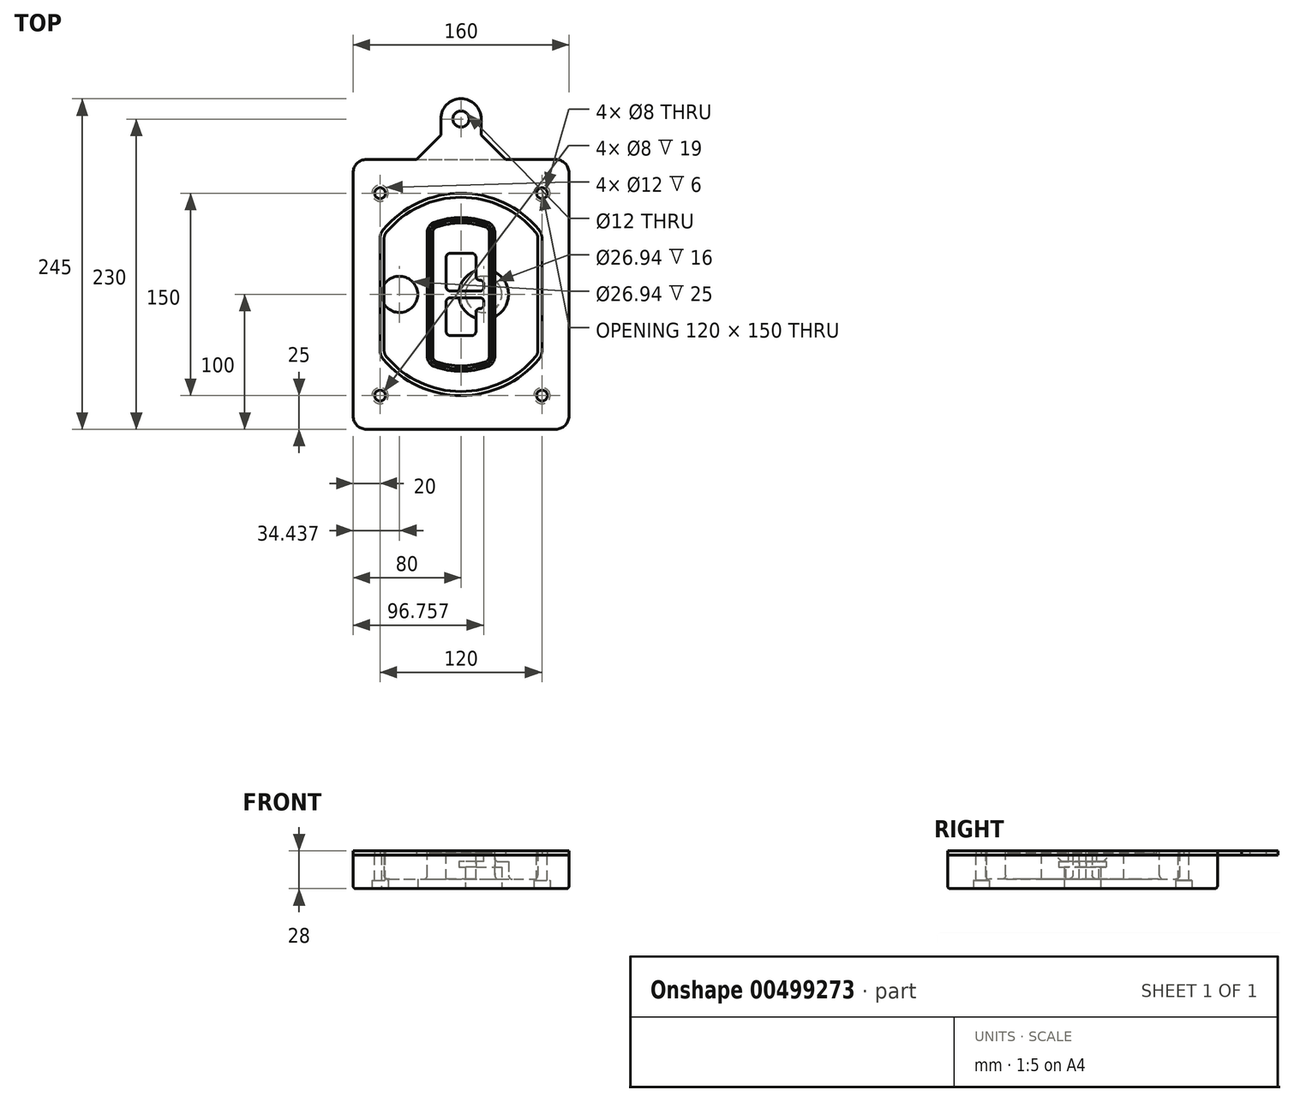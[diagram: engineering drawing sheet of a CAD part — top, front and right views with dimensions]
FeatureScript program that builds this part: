
annotation { "Feature Type Name" : "Feature", "Feature Type Description" : "" }
export const myFeature = defineFeature(function(context is Context, id is Id, definition is map)
    precondition{}
    {
        {
            var Q0;
            Q0=qCreatedBy(makeId("Top.planeOp"),FACE);
            var sketch = newSketch(context, id + "F0", { "sketchPlane" : qUnion([Q0])});
            skPoint(sketch, "E0.rect.middle", {"position": v(0, 0) * mm});
            skLineSegment(sketch, "E1.bottom", {"start": v(-70, -100) * mm, "end": v(70, -100) * mm});
            skLineSegment(sketch, "E1.top", {"start": v(-70, 100) * mm, "end": v(70, 100) * mm});
            skLineSegment(sketch, "E1.left", {"start": v(-80, -90) * mm, "end": v(-80, 90) * mm});
            skLineSegment(sketch, "E1.right", {"start": v(80, -90) * mm, "end": v(80, 90) * mm});
            skLineSegment(sketch, "E2", {"start": v(-80, 100) * mm, "end": v(80, -100) * mm, "construction": true});
            skLineSegment(sketch, "E3", {"start": v(80, 100) * mm, "end": v(-80, -100) * mm, "construction": true});
            skCircle(sketch, "E4", {"center": v(-60, 75) * mm, "radius": 4 * mm});
            skCircle(sketch, "E5", {"center": v(60, 75) * mm, "radius": 4 * mm});
            skCircle(sketch, "E6", {"center": v(60, -75) * mm, "radius": 4 * mm});
            skCircle(sketch, "E7", {"center": v(-60, -75) * mm, "radius": 4 * mm});
            skLineSegment(sketch, "E8", {"start": v(-60, 75) * mm, "end": v(60, 75) * mm, "construction": true});
            skLineSegment(sketch, "E9", {"start": v(60, 75) * mm, "end": v(60, -75) * mm, "construction": true});
            skLineSegment(sketch, "E10", {"start": v(60, -75) * mm, "end": v(-60, -75) * mm, "construction": true});
            skLineSegment(sketch, "E11", {"start": v(-60, -75) * mm, "end": v(-60, 75) * mm, "construction": true});
            skLineSegment(sketch, "E12", {"start": v(-60, 41.53) * mm, "end": v(-60, -41.53) * mm});
            skLineSegment(sketch, "E13", {"start": v(60, 41.53) * mm, "end": v(60, -41.53) * mm});
            skArc(sketch, "E14", {"start": v(57.7, 47.92) * mm, "mid": v(0, 75) * mm, "end": v(-57.7, 47.92) * mm});
            skArc(sketch, "E15", {"start": v(-57.7, -47.92) * mm, "mid": v(0, -75) * mm, "end": v(57.7, -47.92) * mm});
            skLineSegment(sketch, "E16", {"start": v(-60, 0) * mm, "end": v(60, 0) * mm, "construction": true});
            skPoint(sketch, "E17.visualSharp", {"position": v(-60, -45) * mm});
            skArc(sketch, "E17.filletArc", {"start": v(-60, -41.53) * mm, "mid": v(-59.4, -44.93) * mm, "end": v(-57.7, -47.92) * mm});
            skPoint(sketch, "E18.visualSharp", {"position": v(-60, 45) * mm});
            skArc(sketch, "E18.filletArc", {"start": v(-57.7, 47.92) * mm, "mid": v(-59.4, 44.93) * mm, "end": v(-60, 41.53) * mm});
            skPoint(sketch, "E19.visualSharp", {"position": v(60, 45) * mm});
            skArc(sketch, "E19.filletArc", {"start": v(60, 41.53) * mm, "mid": v(59.4, 44.93) * mm, "end": v(57.7, 47.92) * mm});
            skPoint(sketch, "E20.visualSharp", {"position": v(60, -45) * mm});
            skArc(sketch, "E20.filletArc", {"start": v(57.7, -47.92) * mm, "mid": v(59.4, -44.93) * mm, "end": v(60, -41.53) * mm});
            skPoint(sketch, "E21.visualSharp", {"position": v(-80, 100) * mm});
            skArc(sketch, "E21.filletArc", {"start": v(-70, 100) * mm, "mid": v(-77.07, 97.07) * mm, "end": v(-80, 90) * mm});
            skPoint(sketch, "E22.visualSharp", {"position": v(80, 100) * mm});
            skArc(sketch, "E22.filletArc", {"start": v(80, 90) * mm, "mid": v(77.07, 97.07) * mm, "end": v(70, 100) * mm});
            skPoint(sketch, "E23.visualSharp", {"position": v(80, -100) * mm});
            skArc(sketch, "E23.filletArc", {"start": v(70, -100) * mm, "mid": v(77.07, -97.07) * mm, "end": v(80, -90) * mm});
            skPoint(sketch, "E24.visualSharp", {"position": v(-80, -100) * mm});
            skArc(sketch, "E24.filletArc", {"start": v(-80, -90) * mm, "mid": v(-77.07, -97.07) * mm, "end": v(-70, -100) * mm});
            skArc(sketch, "E25.0", {"start": v(57, 41.53) * mm, "mid": v(56.58, 43.91) * mm, "end": v(55.38, 46) * mm});
            skLineSegment(sketch, "E25.1", {"start": v(57, 41.53) * mm, "end": v(57, -41.53) * mm});
            skArc(sketch, "E25.2", {"start": v(55.38, -46) * mm, "mid": v(56.58, -43.91) * mm, "end": v(57, -41.53) * mm});
            skArc(sketch, "E25.3", {"start": v(-55.38, -46) * mm, "mid": v(0, -72) * mm, "end": v(55.38, -46) * mm});
            skArc(sketch, "E25.4", {"start": v(-57, -41.53) * mm, "mid": v(-56.58, -43.91) * mm, "end": v(-55.38, -46) * mm});
            skArc(sketch, "E25.5", {"start": v(55.38, 46) * mm, "mid": v(0, 72) * mm, "end": v(-55.38, 46) * mm});
            skLineSegment(sketch, "E25.6", {"start": v(-57, 41.53) * mm, "end": v(-57, -41.53) * mm});
            skArc(sketch, "E25.7", {"start": v(-55.38, 46) * mm, "mid": v(-56.58, 43.91) * mm, "end": v(-57, 41.53) * mm});
            skArc(sketch, "E26.0", {"start": v(-60.77, 50.48) * mm, "mid": v(-63.17, 46.29) * mm, "end": v(-64, 41.53) * mm});
            skArc(sketch, "E26.1", {"start": v(60.77, 50.48) * mm, "mid": v(0, 79) * mm, "end": v(-60.77, 50.48) * mm});
            skArc(sketch, "E26.2", {"start": v(64, 41.53) * mm, "mid": v(63.17, 46.29) * mm, "end": v(60.77, 50.48) * mm});
            skLineSegment(sketch, "E26.3", {"start": v(64, 41.53) * mm, "end": v(64, -41.53) * mm});
            skArc(sketch, "E26.4", {"start": v(60.77, -50.48) * mm, "mid": v(63.17, -46.29) * mm, "end": v(64, -41.53) * mm});
            skLineSegment(sketch, "E26.5", {"start": v(-64, 41.53) * mm, "end": v(-64, -41.53) * mm});
            skArc(sketch, "E26.6", {"start": v(-60.77, -50.48) * mm, "mid": v(0, -79) * mm, "end": v(60.77, -50.48) * mm});
            skArc(sketch, "E26.7", {"start": v(-64, -41.53) * mm, "mid": v(-63.17, -46.29) * mm, "end": v(-60.77, -50.48) * mm});
            skSolve(sketch);
        }
        {
            var Q0;
            Q0=makeQuery(id+"F0.imprint","IMPRINT",FACE,{"disambiguationData":[TD([[makeQuery(id+"F0.imprint","IMPRINT",EDGE,{"derivedFrom":sQuery(id+"F0.wireOp",EDGE,"E1.bottom")}),1.0]])]});
            var Q1;
            Q1=makeQuery(id+"F0.imprint","IMPRINT",FACE,{"disambiguationData":[TD([[makeQuery(id+"F0.imprint","IMPRINT",EDGE,{"derivedFrom":sQuery(id+"F0.wireOp",EDGE,"E12")}),1.0]])]});
            var Q2;
            Q2=makeQuery(id+"F0.imprint","IMPRINT",FACE,{"disambiguationData":[TD([[makeQuery(id+"F0.imprint","IMPRINT",EDGE,{"derivedFrom":sQuery(id+"F0.wireOp",EDGE,"E25.0")}),1.0]])]});
            var Q3;
            Q3=makeQuery(id+"F0.imprint","IMPRINT",FACE,{"disambiguationData":[TD([[makeQuery(id+"F0.imprint","IMPRINT",EDGE,{"derivedFrom":sQuery(id+"F0.wireOp",EDGE,"E12")}),-1.0]])]});
            extrude(context, id + "F1", {"entities" : qUnion([Q0, Q1, Q2, Q3]), "oppositeDirection" : true, "depth" : 25 * mm});
        }
        {
            var Q0;
            Q0=makeQuery(id+"F0.imprint","IMPRINT",FACE,{"disambiguationData":[TD([[makeQuery(id+"F0.imprint","IMPRINT",EDGE,{"derivedFrom":sQuery(id+"F0.wireOp",EDGE,"E12")}),1.0]])]});
            extrude(context, id + "F2", {"entities" : qUnion([Q0]), "operationType" : NewBodyOperationType.ADD, "depth" : 3 * mm});
        }
        {
            var Q0;
            Q0=makeQuery(id+"F0.imprint","IMPRINT",FACE,{"disambiguationData":[TD([[makeQuery(id+"F0.imprint","IMPRINT",EDGE,{"derivedFrom":sQuery(id+"F0.wireOp",EDGE,"E25.0")}),1.0]])]});
            extrude(context, id + "F3", {"entities" : qUnion([Q0]), "operationType" : NewBodyOperationType.REMOVE, "oppositeDirection" : true, "depth" : 18 * mm});
        }
        {
            var Q0;
            Q0=makeQuery(id+"F2.opExtrude","CAP_FACE",FACE,{"disambiguationData":[OSD([sQuery(id+"F0.wireOp",EDGE,"E12"),sQuery(id+"F0.wireOp",EDGE,"E13"),sQuery(id+"F0.wireOp",EDGE,"E14"),sQuery(id+"F0.wireOp",EDGE,"E15"),sQuery(id+"F0.wireOp",EDGE,"E17.filletArc"),sQuery(id+"F0.wireOp",EDGE,"E18.filletArc"),sQuery(id+"F0.wireOp",EDGE,"E19.filletArc"),sQuery(id+"F0.wireOp",EDGE,"E20.filletArc"),sQuery(id+"F0.wireOp",EDGE,"E25.0"),sQuery(id+"F0.wireOp",EDGE,"E25.1"),sQuery(id+"F0.wireOp",EDGE,"E25.2"),sQuery(id+"F0.wireOp",EDGE,"E25.3"),sQuery(id+"F0.wireOp",EDGE,"E25.4"),sQuery(id+"F0.wireOp",EDGE,"E25.5"),sQuery(id+"F0.wireOp",EDGE,"E25.6"),sQuery(id+"F0.wireOp",EDGE,"E25.7")])],"isStart":false});
            var sketch = newSketch(context, id + "F4", { "sketchPlane" : qUnion([Q0])});
            skArc(sketch, "E27.0", {"start": v(-19.78, -53.46) * mm, "mid": v(0, -57) * mm, "end": v(19.78, -53.46) * mm});
            skArc(sketch, "E28.0", {"start": v(19.78, 53.46) * mm, "mid": v(0, 57) * mm, "end": v(-19.78, 53.46) * mm});
            skLineSegment(sketch, "E29", {"start": v(-25, 45.96) * mm, "end": v(-25, -45.96) * mm});
            skLineSegment(sketch, "E30", {"start": v(25, 45.96) * mm, "end": v(25, -45.96) * mm});
            skLineSegment(sketch, "E31", {"start": v(-25, 51.22) * mm, "end": v(25, 51.22) * mm, "construction": true});
            skLineSegment(sketch, "E32", {"start": v(-25, -51.22) * mm, "end": v(25, -51.22) * mm, "construction": true});
            skPoint(sketch, "E33.visualSharp", {"position": v(-25, 51.22) * mm});
            skArc(sketch, "E33.filletArc", {"start": v(-19.78, 53.46) * mm, "mid": v(-23.57, 50.53) * mm, "end": v(-25, 45.96) * mm});
            skPoint(sketch, "E34.visualSharp", {"position": v(25, 51.22) * mm});
            skArc(sketch, "E34.filletArc", {"start": v(25, 45.96) * mm, "mid": v(23.57, 50.53) * mm, "end": v(19.78, 53.46) * mm});
            skPoint(sketch, "E35.visualSharp", {"position": v(25, -51.22) * mm});
            skArc(sketch, "E35.filletArc", {"start": v(19.78, -53.46) * mm, "mid": v(23.57, -50.53) * mm, "end": v(25, -45.96) * mm});
            skPoint(sketch, "E36.visualSharp", {"position": v(-25, -51.22) * mm});
            skArc(sketch, "E36.filletArc", {"start": v(-25, -45.96) * mm, "mid": v(-23.57, -50.53) * mm, "end": v(-19.78, -53.46) * mm});
            skArc(sketch, "E37.0", {"start": v(55.38, 46) * mm, "mid": v(0, 72) * mm, "end": v(-55.38, 46) * mm});
            skArc(sketch, "E37.1", {"start": v(-55.38, 46) * mm, "mid": v(-56.58, 43.91) * mm, "end": v(-57, 41.53) * mm});
            skLineSegment(sketch, "E37.2", {"start": v(-57, 41.53) * mm, "end": v(-57, -41.53) * mm});
            skArc(sketch, "E37.3", {"start": v(-57, -41.53) * mm, "mid": v(-56.58, -43.91) * mm, "end": v(-55.38, -46) * mm});
            skArc(sketch, "E37.4", {"start": v(-55.38, -46) * mm, "mid": v(0, -72) * mm, "end": v(55.38, -46) * mm});
            skArc(sketch, "E37.5", {"start": v(55.38, -46) * mm, "mid": v(56.58, -43.91) * mm, "end": v(57, -41.53) * mm});
            skLineSegment(sketch, "E37.6", {"start": v(57, 41.53) * mm, "end": v(57, -41.53) * mm});
            skArc(sketch, "E37.7", {"start": v(57, 41.53) * mm, "mid": v(56.58, 43.91) * mm, "end": v(55.38, 46) * mm});
            skLineSegment(sketch, "E38.0", {"start": v(23, 45.96) * mm, "end": v(23, -45.96) * mm});
            skArc(sketch, "E38.1", {"start": v(19.08, -51.58) * mm, "mid": v(21.92, -49.39) * mm, "end": v(23, -45.96) * mm});
            skArc(sketch, "E38.2", {"start": v(-19.08, -51.58) * mm, "mid": v(0, -55) * mm, "end": v(19.08, -51.58) * mm});
            skArc(sketch, "E38.3", {"start": v(-23, -45.96) * mm, "mid": v(-21.92, -49.39) * mm, "end": v(-19.08, -51.58) * mm});
            skLineSegment(sketch, "E38.4", {"start": v(-23, 45.96) * mm, "end": v(-23, -45.96) * mm});
            skArc(sketch, "E38.5", {"start": v(23, 45.96) * mm, "mid": v(21.92, 49.39) * mm, "end": v(19.08, 51.58) * mm});
            skArc(sketch, "E38.6", {"start": v(-19.08, 51.58) * mm, "mid": v(-21.92, 49.39) * mm, "end": v(-23, 45.96) * mm});
            skArc(sketch, "E38.7", {"start": v(19.08, 51.58) * mm, "mid": v(0, 55) * mm, "end": v(-19.08, 51.58) * mm});
            skArc(sketch, "E39.0", {"start": v(21, 45.96) * mm, "mid": v(20.28, 48.24) * mm, "end": v(18.39, 49.7) * mm});
            skLineSegment(sketch, "E39.1", {"start": v(21, 45.96) * mm, "end": v(21, -45.96) * mm});
            skArc(sketch, "E39.2", {"start": v(18.39, -49.7) * mm, "mid": v(20.28, -48.24) * mm, "end": v(21, -45.96) * mm});
            skArc(sketch, "E39.3", {"start": v(-18.39, -49.7) * mm, "mid": v(0, -53) * mm, "end": v(18.39, -49.7) * mm});
            skArc(sketch, "E39.4", {"start": v(-21, -45.96) * mm, "mid": v(-20.28, -48.24) * mm, "end": v(-18.39, -49.7) * mm});
            skArc(sketch, "E39.5", {"start": v(18.39, 49.7) * mm, "mid": v(0, 53) * mm, "end": v(-18.39, 49.7) * mm});
            skLineSegment(sketch, "E39.6", {"start": v(-21, 45.96) * mm, "end": v(-21, -45.96) * mm});
            skArc(sketch, "E39.7", {"start": v(-18.39, 49.7) * mm, "mid": v(-20.28, 48.24) * mm, "end": v(-21, 45.96) * mm});
            skLineSegment(sketch, "E40", {"start": v(-25, 0) * mm, "end": v(25, 0) * mm, "construction": true});
            skLineSegment(sketch, "E41", {"start": v(-11, 5.5) * mm, "end": v(-11, 27.5) * mm});
            skLineSegment(sketch, "E42", {"start": v(-8, 30.5) * mm, "end": v(8, 30.5) * mm});
            skLineSegment(sketch, "E43", {"start": v(11, 27.5) * mm, "end": v(11, 13.5) * mm});
            skLineSegment(sketch, "E44", {"start": v(14, 10.5) * mm, "end": v(14, 10.5) * mm});
            skLineSegment(sketch, "E45", {"start": v(17, 7.5) * mm, "end": v(17, 5.5) * mm});
            skLineSegment(sketch, "E46", {"start": v(14, 2.5) * mm, "end": v(-8, 2.5) * mm});
            skPoint(sketch, "E47.visualSharp", {"position": v(-11, 30.5) * mm});
            skArc(sketch, "E47.filletArc", {"start": v(-8, 30.5) * mm, "mid": v(-10.12, 29.62) * mm, "end": v(-11, 27.5) * mm});
            skPoint(sketch, "E48.visualSharp", {"position": v(11, 30.5) * mm});
            skArc(sketch, "E48.filletArc", {"start": v(11, 27.5) * mm, "mid": v(10.12, 29.62) * mm, "end": v(8, 30.5) * mm});
            skPoint(sketch, "E49.visualSharp", {"position": v(11, 10.5) * mm});
            skArc(sketch, "E49.filletArc", {"start": v(11, 13.5) * mm, "mid": v(11.88, 11.38) * mm, "end": v(14, 10.5) * mm});
            skPoint(sketch, "E50.visualSharp", {"position": v(17, 10.5) * mm});
            skArc(sketch, "E50.filletArc", {"start": v(17, 7.5) * mm, "mid": v(16.12, 9.62) * mm, "end": v(14, 10.5) * mm});
            skPoint(sketch, "E51.visualSharp", {"position": v(17, 2.5) * mm});
            skArc(sketch, "E51.filletArc", {"start": v(14, 2.5) * mm, "mid": v(16.12, 3.38) * mm, "end": v(17, 5.5) * mm});
            skPoint(sketch, "E52.visualSharp", {"position": v(-11, 2.5) * mm});
            skArc(sketch, "E52.filletArc", {"start": v(-11, 5.5) * mm, "mid": v(-10.12, 3.38) * mm, "end": v(-8, 2.5) * mm});
            skLineSegment(sketch, "E53.0.MirrorCS", {"start": v(14, -2.5) * mm, "end": v(-8, -2.5) * mm});
            skArc(sketch, "E54.0.MirrorCS", {"start": v(-11, -5.5) * mm, "mid": v(-10.12, -3.38) * mm, "end": v(-8, -2.5) * mm});
            skLineSegment(sketch, "E55.0.MirrorCS", {"start": v(-11, -5.5) * mm, "end": v(-11, -27.5) * mm});
            skArc(sketch, "E56.0.MirrorCS", {"start": v(-8, -30.5) * mm, "mid": v(-10.12, -29.62) * mm, "end": v(-11, -27.5) * mm});
            skLineSegment(sketch, "E57.0.MirrorCS", {"start": v(-8, -30.5) * mm, "end": v(8, -30.5) * mm});
            skArc(sketch, "E58.0.MirrorCS", {"start": v(11, -27.5) * mm, "mid": v(10.12, -29.62) * mm, "end": v(8, -30.5) * mm});
            skLineSegment(sketch, "E59.0.MirrorCS", {"start": v(11, -27.5) * mm, "end": v(11, -13.5) * mm});
            skArc(sketch, "E60.0.MirrorCS", {"start": v(11, -13.5) * mm, "mid": v(11.88, -11.38) * mm, "end": v(14, -10.5) * mm});
            skArc(sketch, "E61.0.MirrorCS", {"start": v(17, -7.5) * mm, "mid": v(16.12, -9.62) * mm, "end": v(14, -10.5) * mm});
            skLineSegment(sketch, "E62.0.MirrorCS", {"start": v(17, -7.5) * mm, "end": v(17, -5.5) * mm});
            skArc(sketch, "E63.0.MirrorCS", {"start": v(14, -2.5) * mm, "mid": v(16.12, -3.38) * mm, "end": v(17, -5.5) * mm});
            skSolve(sketch);
        }
        {
            var Q0;
            Q0=makeQuery(id+"F4.imprint","IMPRINT",FACE,{"disambiguationData":[TD([[makeQuery(id+"F4.imprint","IMPRINT",EDGE,{"derivedFrom":sQuery(id+"F4.wireOp",EDGE,"E27.0")}),1.0]])]});
            var Q1;
            Q1=makeQuery(id+"F4.imprint","IMPRINT",FACE,{"disambiguationData":[TD([[makeQuery(id+"F4.imprint","IMPRINT",EDGE,{"derivedFrom":sQuery(id+"F4.wireOp",EDGE,"E38.0")}),-1.0]])]});
            var Q2;
            Q2=makeQuery(id+"F4.imprint","IMPRINT",FACE,{"disambiguationData":[TD([[makeQuery(id+"F4.imprint","IMPRINT",EDGE,{"derivedFrom":sQuery(id+"F4.wireOp",EDGE,"E39.0")}),1.0]])]});
            extrude(context, id + "F5", {"entities" : qUnion([Q0, Q1, Q2]), "operationType" : NewBodyOperationType.ADD, "endBound" : BoundingType.UP_TO_NEXT, "oppositeDirection" : true, "depth" : 25 * mm});
        }
        {
            var Q0;
            Q0=makeQuery(id+"F4.imprint","IMPRINT",FACE,{"disambiguationData":[TD([[makeQuery(id+"F4.imprint","IMPRINT",EDGE,{"derivedFrom":sQuery(id+"F4.wireOp",EDGE,"E38.0")}),-1.0]])]});
            extrude(context, id + "F6", {"entities" : qUnion([Q0]), "operationType" : NewBodyOperationType.REMOVE, "oppositeDirection" : true, "depth" : 2 * mm});
        }
        {
            var Q0;
            Q0=makeQuery(id+"F1.opExtrude","CAP_FACE",FACE,{"disambiguationData":[OSD([sQuery(id+"F0.wireOp",EDGE,"E1.bottom"),sQuery(id+"F0.wireOp",EDGE,"E1.top"),sQuery(id+"F0.wireOp",EDGE,"E1.left"),sQuery(id+"F0.wireOp",EDGE,"E1.right"),sQuery(id+"F0.wireOp",EDGE,"E4"),sQuery(id+"F0.wireOp",EDGE,"E5"),sQuery(id+"F0.wireOp",EDGE,"E6"),sQuery(id+"F0.wireOp",EDGE,"E7"),sQuery(id+"F0.wireOp",EDGE,"E21.filletArc"),sQuery(id+"F0.wireOp",EDGE,"E22.filletArc"),sQuery(id+"F0.wireOp",EDGE,"E23.filletArc"),sQuery(id+"F0.wireOp",EDGE,"E24.filletArc")])],"isStart":false});
            var sketch = newSketch(context, id + "F7", { "sketchPlane" : qUnion([Q0])});
            skCircle(sketch, "E64", {"center": v(16.76, 0) * mm, "radius": 13.47 * mm});
            skCircle(sketch, "E65", {"center": v(-45.56, 0) * mm, "radius": 13.47 * mm});
            skLineSegment(sketch, "E66", {"start": v(80, 0) * mm, "end": v(-80, 0) * mm});
            skCircle(sketch, "E67", {"center": v(16.76, 0) * mm, "radius": 18.47 * mm});
            skCircle(sketch, "E68", {"center": v(60, -75) * mm, "radius": 6 * mm});
            skCircle(sketch, "E69", {"center": v(-60, -75) * mm, "radius": 6 * mm});
            skCircle(sketch, "E70", {"center": v(-60, 75) * mm, "radius": 6 * mm});
            skCircle(sketch, "E71", {"center": v(60, 75) * mm, "radius": 6 * mm});
            skSolve(sketch);
        }
        {
            var Q0;
            {var subQ1=sQuery(id+"F7.wireOp",EDGE,"E66");var subQ4=sQuery(id+"F7.wireOp",EDGE,"E64");var subQ6=makeQuery(id+"F7.imprint","INTERSECT",VERTEX,{"disambiguationData":[OD(0.0)],"derivedFrom":[subQ4,subQ1]});Q0=makeQuery(id+"F7.imprint","IMPRINT",FACE,{"disambiguationData":[TD([[makeQuery(id+"F7.imprint","IMPRINT",EDGE,{"disambiguationData":[TD([[subQ6,-1.0]])],"derivedFrom":subQ4}),-1.0]])]});}
            var Q1;
            {var subQ0=sQuery(id+"F7.wireOp",EDGE,"E66");var subQ1=sQuery(id+"F7.wireOp",EDGE,"E64");var subQ3=makeQuery(id+"F7.imprint","INTERSECT",VERTEX,{"disambiguationData":[OD(0.0)],"derivedFrom":[subQ1,subQ0]});Q1=makeQuery(id+"F7.imprint","IMPRINT",FACE,{"disambiguationData":[TD([[makeQuery(id+"F7.imprint","IMPRINT",EDGE,{"disambiguationData":[TD([[subQ3,-1.0]])],"derivedFrom":subQ1}),1.0]])]});}
            var Q2;
            {var subQ0=sQuery(id+"F7.wireOp",EDGE,"E66");var subQ1=sQuery(id+"F7.wireOp",EDGE,"E64");var subQ3=makeQuery(id+"F7.imprint","INTERSECT",VERTEX,{"disambiguationData":[OD(0.0)],"derivedFrom":[subQ1,subQ0]});Q2=makeQuery(id+"F7.imprint","IMPRINT",FACE,{"disambiguationData":[TD([[makeQuery(id+"F7.imprint","IMPRINT",EDGE,{"disambiguationData":[TD([[subQ3,1.0]])],"derivedFrom":subQ1}),1.0]])]});}
            var Q3;
            {var subQ1=sQuery(id+"F7.wireOp",EDGE,"E66");var subQ4=sQuery(id+"F7.wireOp",EDGE,"E64");var subQ6=makeQuery(id+"F7.imprint","INTERSECT",VERTEX,{"disambiguationData":[OD(0.0)],"derivedFrom":[subQ4,subQ1]});Q3=makeQuery(id+"F7.imprint","IMPRINT",FACE,{"disambiguationData":[TD([[makeQuery(id+"F7.imprint","IMPRINT",EDGE,{"disambiguationData":[TD([[subQ6,1.0]])],"derivedFrom":subQ4}),-1.0]])]});}
            extrude(context, id + "F8", {"entities" : qUnion([Q0, Q1, Q2, Q3]), "operationType" : NewBodyOperationType.ADD, "oppositeDirection" : true, "depth" : 20 * mm});
        }
        {
            var Q0;
            {var subQ0=sQuery(id+"F7.wireOp",EDGE,"E66");var subQ1=sQuery(id+"F7.wireOp",EDGE,"E64");var subQ3=makeQuery(id+"F7.imprint","INTERSECT",VERTEX,{"disambiguationData":[OD(0.0)],"derivedFrom":[subQ1,subQ0]});Q0=makeQuery(id+"F7.imprint","IMPRINT",FACE,{"disambiguationData":[TD([[makeQuery(id+"F7.imprint","IMPRINT",EDGE,{"disambiguationData":[TD([[subQ3,-1.0]])],"derivedFrom":subQ1}),1.0]])]});}
            var Q1;
            {var subQ0=sQuery(id+"F7.wireOp",EDGE,"E66");var subQ1=sQuery(id+"F7.wireOp",EDGE,"E64");var subQ3=makeQuery(id+"F7.imprint","INTERSECT",VERTEX,{"disambiguationData":[OD(0.0)],"derivedFrom":[subQ1,subQ0]});Q1=makeQuery(id+"F7.imprint","IMPRINT",FACE,{"disambiguationData":[TD([[makeQuery(id+"F7.imprint","IMPRINT",EDGE,{"disambiguationData":[TD([[subQ3,1.0]])],"derivedFrom":subQ1}),1.0]])]});}
            extrude(context, id + "F9", {"entities" : qUnion([Q0, Q1]), "operationType" : NewBodyOperationType.REMOVE, "oppositeDirection" : true, "depth" : 16 * mm});
        }
        {
            var Q0;
            {var subQ0=sQuery(id+"F7.wireOp",EDGE,"E66");var subQ1=sQuery(id+"F7.wireOp",EDGE,"E65");var subQ3=makeQuery(id+"F7.imprint","INTERSECT",VERTEX,{"disambiguationData":[OD(0.0)],"derivedFrom":[subQ1,subQ0]});Q0=makeQuery(id+"F7.imprint","IMPRINT",FACE,{"disambiguationData":[TD([[makeQuery(id+"F7.imprint","IMPRINT",EDGE,{"disambiguationData":[TD([[subQ3,-1.0]])],"derivedFrom":subQ1}),1.0]])]});}
            var Q1;
            {var subQ0=sQuery(id+"F7.wireOp",EDGE,"E66");var subQ1=sQuery(id+"F7.wireOp",EDGE,"E65");var subQ3=makeQuery(id+"F7.imprint","INTERSECT",VERTEX,{"disambiguationData":[OD(0.0)],"derivedFrom":[subQ1,subQ0]});Q1=makeQuery(id+"F7.imprint","IMPRINT",FACE,{"disambiguationData":[TD([[makeQuery(id+"F7.imprint","IMPRINT",EDGE,{"disambiguationData":[TD([[subQ3,1.0]])],"derivedFrom":subQ1}),1.0]])]});}
            extrude(context, id + "F10", {"entities" : qUnion([Q0, Q1]), "operationType" : NewBodyOperationType.REMOVE, "oppositeDirection" : true, "depth" : 25 * mm});
        }
        {
            var Q0;
            Q0=makeQuery(id+"F7.imprint","IMPRINT",FACE,{"disambiguationData":[TD([[makeQuery(id+"F7.imprint","IMPRINT",EDGE,{"derivedFrom":sQuery(id+"F7.wireOp",EDGE,"E68")}),1.0]])]});
            var Q1;
            Q1=makeQuery(id+"F7.imprint","IMPRINT",FACE,{"disambiguationData":[TD([[makeQuery(id+"F7.imprint","IMPRINT",EDGE,{"derivedFrom":makeQuery(id+"F1.opExtrude","CAP_EDGE",EDGE,{"disambiguationData":[OSD([sQuery(id+"F0.wireOp",EDGE,"E5")])],"isStart":false})}),-1.0]])]});
            var Q2;
            Q2=makeQuery(id+"F7.imprint","IMPRINT",FACE,{"disambiguationData":[TD([[makeQuery(id+"F7.imprint","IMPRINT",EDGE,{"derivedFrom":sQuery(id+"F7.wireOp",EDGE,"E69")}),1.0]])]});
            var Q3;
            Q3=makeQuery(id+"F7.imprint","IMPRINT",FACE,{"disambiguationData":[TD([[makeQuery(id+"F7.imprint","IMPRINT",EDGE,{"derivedFrom":makeQuery(id+"F1.opExtrude","CAP_EDGE",EDGE,{"disambiguationData":[OSD([sQuery(id+"F0.wireOp",EDGE,"E4")])],"isStart":false})}),-1.0]])]});
            var Q4;
            Q4=makeQuery(id+"F7.imprint","IMPRINT",FACE,{"disambiguationData":[TD([[makeQuery(id+"F7.imprint","IMPRINT",EDGE,{"derivedFrom":sQuery(id+"F7.wireOp",EDGE,"E70")}),1.0]])]});
            var Q5;
            Q5=makeQuery(id+"F7.imprint","IMPRINT",FACE,{"disambiguationData":[TD([[makeQuery(id+"F7.imprint","IMPRINT",EDGE,{"derivedFrom":makeQuery(id+"F1.opExtrude","CAP_EDGE",EDGE,{"disambiguationData":[OSD([sQuery(id+"F0.wireOp",EDGE,"E7")])],"isStart":false})}),-1.0]])]});
            var Q6;
            Q6=makeQuery(id+"F7.imprint","IMPRINT",FACE,{"disambiguationData":[TD([[makeQuery(id+"F7.imprint","IMPRINT",EDGE,{"derivedFrom":sQuery(id+"F7.wireOp",EDGE,"E71")}),1.0]])]});
            var Q7;
            Q7=makeQuery(id+"F7.imprint","IMPRINT",FACE,{"disambiguationData":[TD([[makeQuery(id+"F7.imprint","IMPRINT",EDGE,{"derivedFrom":makeQuery(id+"F1.opExtrude","CAP_EDGE",EDGE,{"disambiguationData":[OSD([sQuery(id+"F0.wireOp",EDGE,"E6")])],"isStart":false})}),-1.0]])]});
            extrude(context, id + "F11", {"entities" : qUnion([Q0, Q1, Q2, Q3, Q4, Q5, Q6, Q7]), "operationType" : NewBodyOperationType.REMOVE, "oppositeDirection" : true, "depth" : 6 * mm});
        }
        {
            var Q0;
            Q0=makeQuery(id+"F9.boolean.opBoolean","COPY",FACE,{"derivedFrom":makeQuery(id+"F9.opExtrude","CAP_FACE",FACE,{"disambiguationData":[OSD([sQuery(id+"F7.wireOp",EDGE,"E64")])],"isStart":false})});
            var sketch = newSketch(context, id + "F12", { "sketchPlane" : qUnion([Q0])});
            skArc(sketch, "E72.0", {"start": v(11, 17.55) * mm, "mid": v(2.57, 11.82) * mm, "end": v(-1.54, 2.5) * mm});
            skArc(sketch, "E72.1", {"start": v(-1.54, -2.5) * mm, "mid": v(2.57, -11.82) * mm, "end": v(11, -17.55) * mm});
            skLineSegment(sketch, "E73", {"start": v(-1.54, -2.5) * mm, "end": v(14, -2.5) * mm});
            skLineSegment(sketch, "E74.0", {"start": v(14, 2.5) * mm, "end": v(-1.54, 2.5) * mm});
            skArc(sketch, "E74.1", {"start": v(14, 2.5) * mm, "mid": v(16.12, 3.38) * mm, "end": v(17, 5.5) * mm});
            skLineSegment(sketch, "E74.2", {"start": v(17, 7.5) * mm, "end": v(17, 5.5) * mm});
            skArc(sketch, "E74.3", {"start": v(17, 7.5) * mm, "mid": v(16.12, 9.62) * mm, "end": v(14, 10.5) * mm});
            skArc(sketch, "E74.4", {"start": v(11, 13.5) * mm, "mid": v(11.88, 11.38) * mm, "end": v(14, 10.5) * mm});
            skLineSegment(sketch, "E74.5", {"start": v(11, 17.55) * mm, "end": v(11, 13.5) * mm});
            skLineSegment(sketch, "E74.7", {"start": v(14, -2.5) * mm, "end": v(-1.54, -2.5) * mm});
            skArc(sketch, "E74.8", {"start": v(14, -2.5) * mm, "mid": v(16.12, -3.38) * mm, "end": v(17, -5.5) * mm});
            skLineSegment(sketch, "E74.9", {"start": v(17, -7.5) * mm, "end": v(17, -5.5) * mm});
            skArc(sketch, "E74.10", {"start": v(17, -7.5) * mm, "mid": v(16.12, -9.62) * mm, "end": v(14, -10.5) * mm});
            skArc(sketch, "E74.11", {"start": v(11, -13.5) * mm, "mid": v(11.88, -11.38) * mm, "end": v(14, -10.5) * mm});
            skLineSegment(sketch, "E74.12", {"start": v(11, -17.55) * mm, "end": v(11, -13.5) * mm});
            skPoint(sketch, "E75.orphan", {"position": v(11, -27.5) * mm});
            skPoint(sketch, "E76.orphan", {"position": v(-8, -2.5) * mm});
            skPoint(sketch, "E77.orphan", {"position": v(-8, 2.5) * mm});
            skPoint(sketch, "E78.orphan", {"position": v(11, 27.5) * mm});
            skSolve(sketch);
        }
        {
            var Q0;
            {var subQ7=sQuery(id+"F12.wireOp",EDGE,"E72.0");var subQ14=sQuery(id+"F12.wireOp",EDGE,"E72.1");var subQ16=sQuery(id+"F12.wireOp",EDGE,"E74.1");var subQ18=sQuery(id+"F12.wireOp",EDGE,"E74.8");Q0=qUnion([makeQuery(id+"F12.imprint","IMPRINT",FACE,{"disambiguationData":[TD([[makeQuery(id+"F12.imprint","IMPRINT",EDGE,{"derivedFrom":subQ7}),1.0]])]}),makeQuery(id+"F12.imprint","IMPRINT",FACE,{"disambiguationData":[TD([[makeQuery(id+"F12.imprint","IMPRINT",EDGE,{"derivedFrom":subQ14}),1.0]])]}),makeQuery(id+"F12.imprint","IMPRINT",FACE,{"disambiguationData":[TD([[makeQuery(id+"F12.imprint","IMPRINT",EDGE,{"derivedFrom":subQ16}),1.0]])]}),makeQuery(id+"F12.imprint","IMPRINT",FACE,{"disambiguationData":[TD([[makeQuery(id+"F12.imprint","IMPRINT",EDGE,{"derivedFrom":subQ18}),-1.0]])]})]);}
            var Q1;
            Q1=makeQuery(id+"F5.boolean.opBoolean","SPLIT",FACE,{"disambiguationData":[TD([makeQuery(id+"F5.opExtrude","SWEPT_FACE",FACE,{"disambiguationData":[OSD([sQuery(id+"F4.wireOp",EDGE,"E41")])]})])],"derivedFrom":makeQuery(id+"F3.boolean.opBoolean","COPY",FACE,{"derivedFrom":makeQuery(id+"F3.opExtrude","CAP_FACE",FACE,{"disambiguationData":[OSD([sQuery(id+"F0.wireOp",EDGE,"E25.0"),sQuery(id+"F0.wireOp",EDGE,"E25.1"),sQuery(id+"F0.wireOp",EDGE,"E25.2"),sQuery(id+"F0.wireOp",EDGE,"E25.3"),sQuery(id+"F0.wireOp",EDGE,"E25.4"),sQuery(id+"F0.wireOp",EDGE,"E25.5"),sQuery(id+"F0.wireOp",EDGE,"E25.6"),sQuery(id+"F0.wireOp",EDGE,"E25.7")])],"isStart":false})})});
            extrude(context, id + "F13", {"entities" : qUnion([Q0]), "operationType" : NewBodyOperationType.REMOVE, "endBound" : BoundingType.UP_TO_SURFACE, "endBoundEntityFace" : qUnion([Q1]), "depth" : 25 * mm});
        }
        {
            var Q0;
            Q0=makeQuery(id+"F3.boolean.opBoolean","COPY",EDGE,{"derivedFrom":makeQuery(id+"F3.opExtrude","CAP_EDGE",EDGE,{"disambiguationData":[OSD([sQuery(id+"F0.wireOp",EDGE,"E25.6")])],"isStart":false})});
            var Q1;
            Q1=makeQuery(id+"F8.boolean.opBoolean","INTERSECT",EDGE,{"derivedFrom":[makeQuery(id+"F5.opExtrude","SWEPT_FACE",FACE,{"disambiguationData":[OSD([sQuery(id+"F4.wireOp",EDGE,"E30")])]}),makeQuery(id+"F8.opExtrude","CAP_FACE",FACE,{"disambiguationData":[OSD([sQuery(id+"F7.wireOp",EDGE,"E67")])],"isStart":false})]});
            var Q2;
            Q2=makeQuery(id+"F8.boolean.opBoolean","INTERSECT",EDGE,{"disambiguationData":[OD(1.0)],"derivedFrom":[makeQuery(id+"F5.opExtrude","SWEPT_FACE",FACE,{"disambiguationData":[OSD([sQuery(id+"F4.wireOp",EDGE,"E30")])]}),makeQuery(id+"F8.opExtrude","SWEPT_FACE",FACE,{"disambiguationData":[OSD([sQuery(id+"F7.wireOp",EDGE,"E67")])]})]});
            var Q3;
            {var subQ0=sQuery(id+"F4.wireOp",EDGE,"E30");Q3=makeQuery(id+"F8.boolean.opBoolean","SPLIT",EDGE,{"disambiguationData":[TD([makeQuery(id+"F5.opExtrude","SWEPT_FACE",FACE,{"disambiguationData":[OSD([sQuery(id+"F4.wireOp",EDGE,"E35.filletArc")])]})])],"derivedFrom":makeQuery(id+"F5.opExtrude","CAP_EDGE",EDGE,{"disambiguationData":[OSD([subQ0])],"isStart":false})});}
            var Q4;
            {var subQ0=sQuery(id+"F0.wireOp",EDGE,"E25.7");var subQ1=sQuery(id+"F0.wireOp",EDGE,"E25.1");var subQ2=sQuery(id+"F0.wireOp",EDGE,"E25.6");var subQ3=sQuery(id+"F0.wireOp",EDGE,"E25.5");var subQ4=sQuery(id+"F0.wireOp",EDGE,"E25.4");var subQ5=sQuery(id+"F0.wireOp",EDGE,"E25.0");var subQ6=sQuery(id+"F0.wireOp",EDGE,"E25.2");var subQ7=sQuery(id+"F0.wireOp",EDGE,"E25.3");Q4=makeQuery(id+"F8.boolean.opBoolean","INTERSECT",EDGE,{"derivedFrom":[makeQuery(id+"F5.boolean.opBoolean","SPLIT",FACE,{"disambiguationData":[TD([makeQuery(id+"F2.opExtrude","SWEPT_FACE",FACE,{"disambiguationData":[OSD([subQ5])]})])],"derivedFrom":makeQuery(id+"F3.boolean.opBoolean","COPY",FACE,{"derivedFrom":makeQuery(id+"F3.opExtrude","CAP_FACE",FACE,{"disambiguationData":[OSD([subQ5,subQ1,subQ6,subQ7,subQ4,subQ3,subQ2,subQ0])],"isStart":false})})}),makeQuery(id+"F8.opExtrude","SWEPT_FACE",FACE,{"disambiguationData":[OSD([sQuery(id+"F7.wireOp",EDGE,"E67")])]})]});}
            var Q5;
            Q5=makeQuery(id+"F8.boolean.opBoolean","INTERSECT",EDGE,{"disambiguationData":[OD(0.0)],"derivedFrom":[makeQuery(id+"F5.opExtrude","SWEPT_FACE",FACE,{"disambiguationData":[OSD([sQuery(id+"F4.wireOp",EDGE,"E30")])]}),makeQuery(id+"F8.opExtrude","SWEPT_FACE",FACE,{"disambiguationData":[OSD([sQuery(id+"F7.wireOp",EDGE,"E67")])]})]});
            fillet(context, id + "F14", {"entities" : qUnion([Q0, Q1, Q2, Q3, Q4, Q5]), "radius" : 3 * mm, "tangentPropagation" : true, "allowEdgeOverflow" : false});
        }
        {
            var Q0;
            Q0=makeQuery(id+"F1.opExtrude","CAP_EDGE",EDGE,{"disambiguationData":[OSD([sQuery(id+"F0.wireOp",EDGE,"E1.bottom")])],"isStart":false});
            fillet(context, id + "F15", {"entities" : qUnion([Q0]), "radius" : 2 * mm, "tangentPropagation" : true, "allowEdgeOverflow" : false});
        }
        {
            var Q0;
            {var subQ0=sQuery(id+"F0.wireOp",EDGE,"E21.filletArc");var subQ1=sQuery(id+"F0.wireOp",EDGE,"E7");var subQ2=sQuery(id+"F0.wireOp",EDGE,"E6");var subQ3=sQuery(id+"F0.wireOp",EDGE,"E5");var subQ4=sQuery(id+"F0.wireOp",EDGE,"E4");var subQ5=sQuery(id+"F0.wireOp",EDGE,"E22.filletArc");var subQ6=sQuery(id+"F0.wireOp",EDGE,"E1.bottom");var subQ7=sQuery(id+"F0.wireOp",EDGE,"E1.right");var subQ8=sQuery(id+"F0.wireOp",EDGE,"E1.top");var subQ9=sQuery(id+"F0.wireOp",EDGE,"E1.left");var subQ10=sQuery(id+"F0.wireOp",EDGE,"E23.filletArc");var subQ11=sQuery(id+"F0.wireOp",EDGE,"E24.filletArc");Q0=makeQuery(id+"F2.boolean.opBoolean","SPLIT",FACE,{"disambiguationData":[TD([makeQuery(id+"F1.opExtrude","SWEPT_FACE",FACE,{"disambiguationData":[OSD([subQ6])]})])],"derivedFrom":makeQuery(id+"F1.opExtrude","CAP_FACE",FACE,{"disambiguationData":[OSD([subQ6,subQ8,subQ9,subQ7,subQ4,subQ3,subQ2,subQ1,subQ0,subQ5,subQ10,subQ11])],"isStart":true})});}
            var sketch = newSketch(context, id + "F16", { "sketchPlane" : qUnion([Q0])});
            skLineSegment(sketch, "E79", {"start": v(0, 100) * mm, "end": v(0, 130) * mm, "construction": true});
            skCircle(sketch, "E80", {"center": v(0, 130) * mm, "radius": 6 * mm});
            skArc(sketch, "E81", {"start": v(15, 130) * mm, "mid": v(0, 145) * mm, "end": v(-15, 130) * mm});
            skLineSegment(sketch, "E82", {"start": v(-15, 130) * mm, "end": v(-15, 118) * mm});
            skLineSegment(sketch, "E83", {"start": v(-15, 118) * mm, "end": v(-33, 100) * mm});
            skLineSegment(sketch, "E84", {"start": v(15, 130) * mm, "end": v(15, 118) * mm});
            skLineSegment(sketch, "E85", {"start": v(15, 118) * mm, "end": v(33, 100) * mm});
            skLineSegment(sketch, "E86", {"start": v(-80, 0) * mm, "end": v(80, 0) * mm, "construction": true});
            skArc(sketch, "E87.MirrorCS", {"start": v(15, -130) * mm, "mid": v(0, -145) * mm, "end": v(-15, -130) * mm});
            skLineSegment(sketch, "E88.MirrorCS", {"start": v(-15, -130) * mm, "end": v(-15, -118) * mm});
            skLineSegment(sketch, "E89.MirrorCS", {"start": v(-15, -118) * mm, "end": v(-33, -100) * mm});
            skLineSegment(sketch, "E90.MirrorCS", {"start": v(15, -118) * mm, "end": v(33, -100) * mm});
            skLineSegment(sketch, "E91.MirrorCS", {"start": v(15, -130) * mm, "end": v(15, -118) * mm});
            skCircle(sketch, "E92.MirrorC", {"center": v(0, -130) * mm, "radius": 6 * mm});
            skLineSegment(sketch, "E93.MirrorCS", {"start": v(0, -100) * mm, "end": v(0, -130) * mm, "construction": true});
            skSolve(sketch);
        }
        {
            var Q0;
            Q0=makeQuery(id+"F16.imprint","IMPRINT",FACE,{"disambiguationData":[TD([[makeQuery(id+"F16.imprint","IMPRINT",EDGE,{"derivedFrom":sQuery(id+"F16.wireOp",EDGE,"E80")}),-1.0]])]});
            var Q1;
            Q1=makeQuery(id+"F16.imprint","IMPRINT",FACE,{"disambiguationData":[TD([[makeQuery(id+"F16.imprint","IMPRINT",EDGE,{"derivedFrom":sQuery(id+"F16.wireOp",EDGE,"E87.MirrorCS")}),-1.0]])]});
            var Q2;
            Q2=makeQuery(id+"F16.imprint","IMPRINT",FACE,{"disambiguationData":[TD([[makeQuery(id+"F16.imprint","IMPRINT",EDGE,{"derivedFrom":makeQuery(id+"F1.opExtrude","CAP_EDGE",EDGE,{"disambiguationData":[OSD([sQuery(id+"F0.wireOp",EDGE,"E1.left")])],"isStart":true})}),-1.0]])]});
            var Q3;
            Q3=makeQuery(id+"F2.opExtrude","CAP_FACE",FACE,{"disambiguationData":[OSD([sQuery(id+"F0.wireOp",EDGE,"E12"),sQuery(id+"F0.wireOp",EDGE,"E13"),sQuery(id+"F0.wireOp",EDGE,"E14"),sQuery(id+"F0.wireOp",EDGE,"E15"),sQuery(id+"F0.wireOp",EDGE,"E17.filletArc"),sQuery(id+"F0.wireOp",EDGE,"E18.filletArc"),sQuery(id+"F0.wireOp",EDGE,"E19.filletArc"),sQuery(id+"F0.wireOp",EDGE,"E20.filletArc"),sQuery(id+"F0.wireOp",EDGE,"E25.0"),sQuery(id+"F0.wireOp",EDGE,"E25.1"),sQuery(id+"F0.wireOp",EDGE,"E25.2"),sQuery(id+"F0.wireOp",EDGE,"E25.3"),sQuery(id+"F0.wireOp",EDGE,"E25.4"),sQuery(id+"F0.wireOp",EDGE,"E25.5"),sQuery(id+"F0.wireOp",EDGE,"E25.6"),sQuery(id+"F0.wireOp",EDGE,"E25.7")])],"isStart":false});
            extrude(context, id + "F17", {"entities" : qUnion([Q0, Q1, Q2]), "endBound" : BoundingType.UP_TO_SURFACE, "endBoundEntityFace" : qUnion([Q3]), "depth" : 25 * mm});
        }
    });
